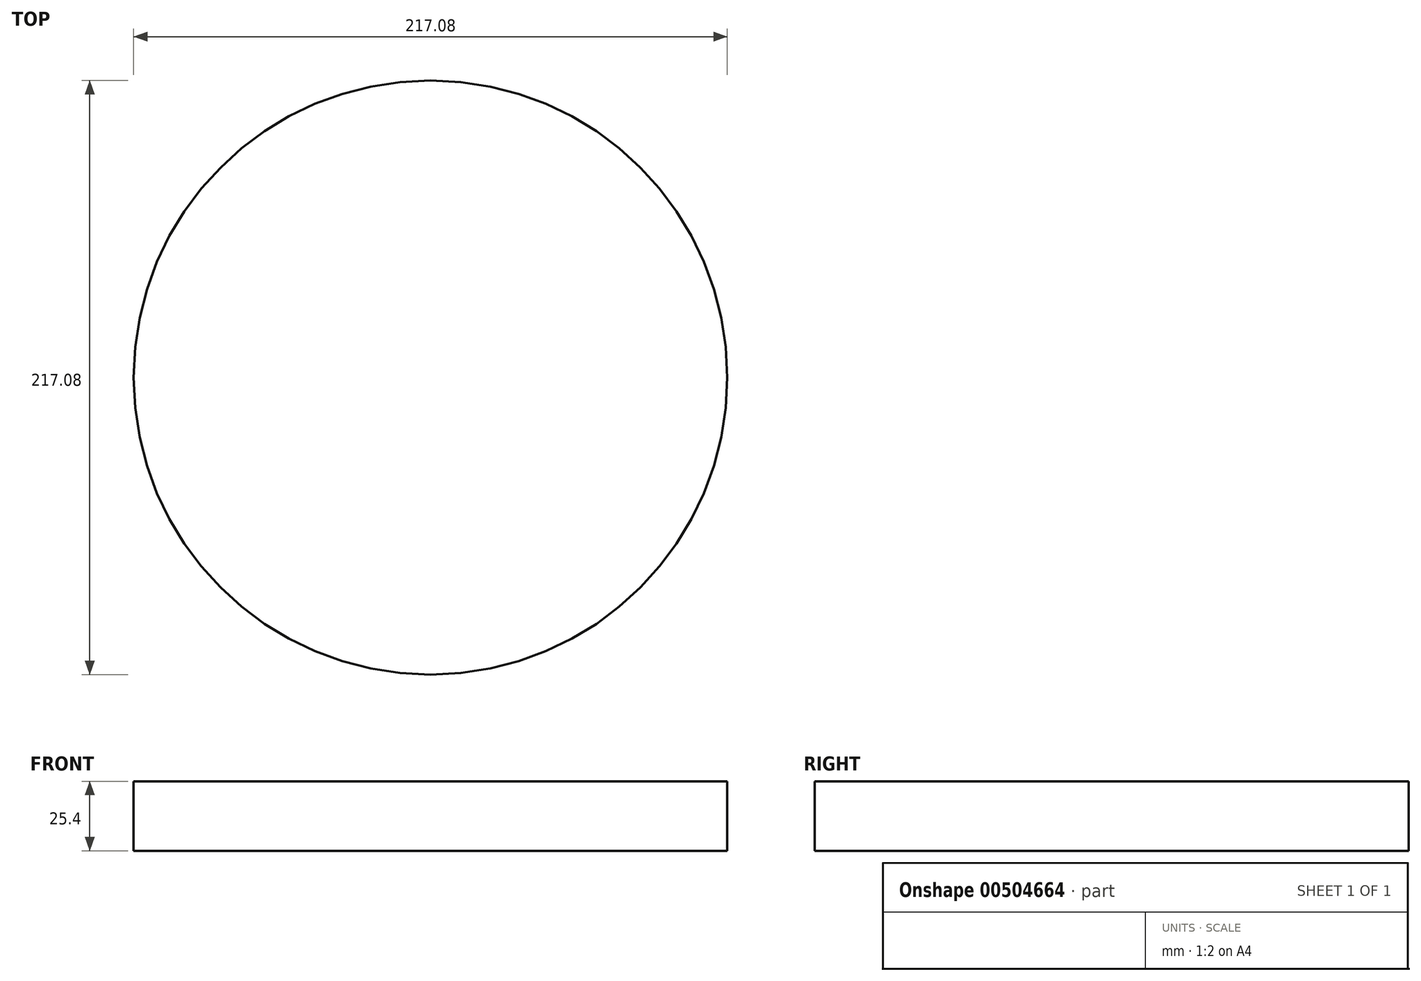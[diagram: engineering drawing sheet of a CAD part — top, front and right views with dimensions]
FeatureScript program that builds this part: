
annotation { "Feature Type Name" : "Feature", "Feature Type Description" : "" }
export const myFeature = defineFeature(function(context is Context, id is Id, definition is map)
    precondition{}
    {
        {
            var Q0;
            Q0=qCreatedBy(makeId("Top.planeOp"),FACE);
            var sketch = newSketch(context, id + "F0", { "sketchPlane" : qUnion([Q0])});
            skLineSegment(sketch, "E0", {"start": v(0, 0) * mm, "end": v(0, 61.42) * mm});
            skLineSegment(sketch, "E1", {"start": v(0, 0) * mm, "end": v(69.52, 0) * mm});
            skSolve(sketch);
        }
        {
            var Q0;
            Q0=qCreatedBy(makeId("Top.planeOp"),FACE);
            var sketch = newSketch(context, id + "F1", { "sketchPlane" : qUnion([Q0])});
            skCircle(sketch, "E2", {"center": v(0, 0) * mm, "radius": 108.54 * mm});
            skSolve(sketch);
        }
        {
            var Q0;
            Q0 = qSketchRegion(id + "F1", true);
            var sketch = newSketch(context, id + "F2", { "sketchPlane" : qUnion([Q0])});
            skLineSegment(sketch, "E3", {"start": v(0, -107.37) * mm, "end": v(0, 0) * mm});
            skLineSegment(sketch, "E4", {"start": v(0, 0) * mm, "end": v(105.25, 0) * mm});
            skLineSegment(sketch, "E5", {"start": v(105.25, 0) * mm, "end": v(0, 0) * mm});
            skSolve(sketch);
        }
        {
            var Q0;
            Q0=makeQuery(id+"F2.imprint","IMPRINT",FACE,{"disambiguationData":[TD([[makeQuery(id+"F2.imprint","IMPRINT",EDGE,{"derivedFrom":makeQuery(id+"F1.imprint","IMPRINT",EDGE,{"derivedFrom":sQuery(id+"F1.wireOp",EDGE,"E2")})}),1.0]])]});
            extrude(context, id + "F3", {"entities" : qUnion([Q0]), "depth" : 25.4 * mm, "offsetDistance" : 25.4 * mm});
        }
    });
